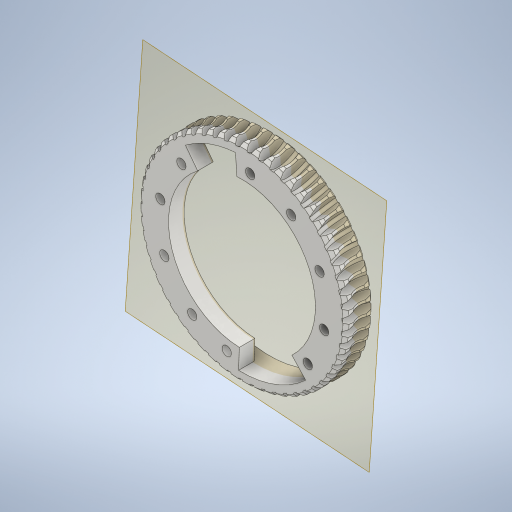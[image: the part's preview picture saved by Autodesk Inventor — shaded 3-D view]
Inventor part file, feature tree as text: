
AUTODESK INVENTOR PART (.ipt)
format: ipt  version: 2023.1 (Build 271208000, 208)  size: 3,268,608 bytes
history: native  units: mm (DEFAULTED — no unit token found)
features: other x8, sketch x5, plane x4, extrude x2, hole x2, pattern_circular x1
ambient origin geometry x5: Origin, X Axis, Y Axis, Z Axis, Center Point
bodies: Solid1 (feature_tree)
feature tree (22):
  other  "Tooth Plane"
  other  "Base Body Sketch"
  other  "Base Body"
  other  "Base Body2"
  plane  "Work Plane13"
  other  "Tooth"
  pattern_circular  "Tooth Pattern"  [2 undecoded]
  plane  "Work Plane14"
  plane  "Work Plane15"
  extrude  "Extrusion1"  Depth=7.0mm
  plane  "Work Plane16"
  extrude  "Extrusion3"  TaperAngle=90.0deg  [1 undecoded]
  hole  "Hole3"  [1 undecoded]
  hole  "Hole4"  [1 undecoded]
  other  "Tooth Sketch"
  sketch  "Sketch8"  dims[d35=90.0deg]
  other  "Srf1"
  sketch  "Sketch9"  dims[d37=-1.106572mm]
  sketch  "Sketch11"  dims[d38=51.477061mm]
  sketch  "Sketch12"  dims[d39=3.490659mm]
  sketch  "Sketch13"  dims[d40=5.28mm d41=7.2mm d42=1.507964mm d43=90.0deg d44=550.0mm d46=360.0deg d50=7.979253mm d68=51.477061mm d69=0.0mm d73=0.0mm d75=0.571199mm d77=88.0mm d78=12.6mm d79=0.0mm d80=0.0mm d81=0.0mm d82=0.0mm d83=0.571199mm d84=0.0mm d85=180.0deg d86=51.477061mm d87=93.354122mm d89=11.2mm d90=90.0deg d92=12.6mm d93=51.477061mm d94=21.25mm d95=0.0mm d98=7.0mm d99=0.0mm d100=4.2mm d101=6.0mm d102=4.0mm d103=2.0mm d104=90.0deg d105=8.0mm d106=0.0mm d107=4.2mm d108=6.0mm d109=4.0mm d110=2.0mm d111=90.0deg d112=8.0mm d113=0.0mm]
  other  "Pitch Diameter"
note: 5 required parameter values undecoded (feature->parameter linkage not recoverable at this tier; creation-order binding heuristic only, values carry confidence <= 0.55)
